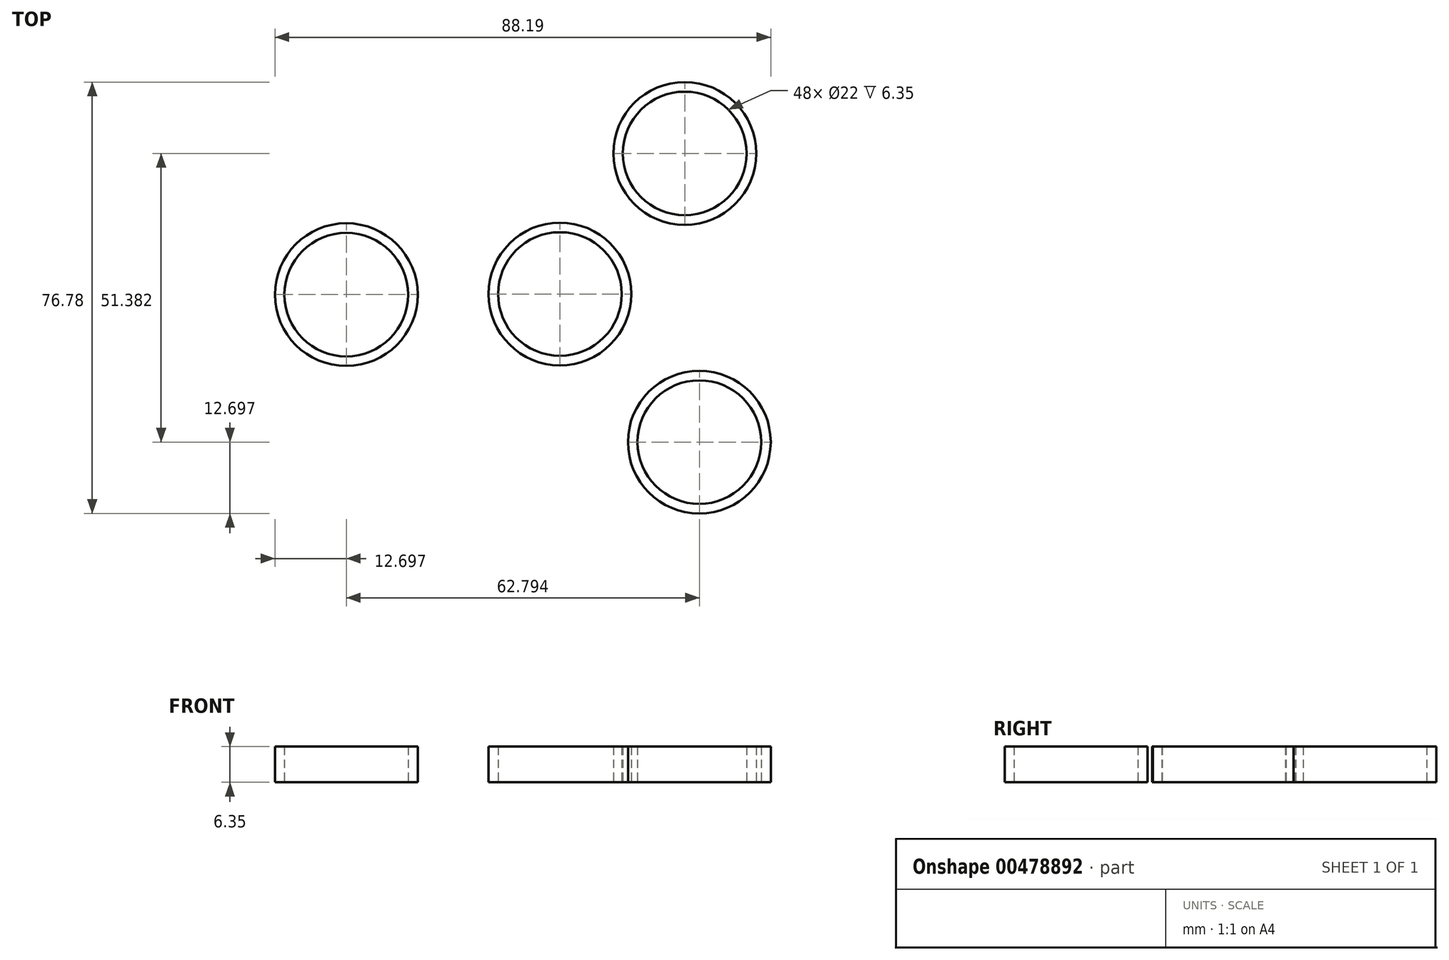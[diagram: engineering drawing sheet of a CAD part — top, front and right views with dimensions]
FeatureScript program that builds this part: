
annotation { "Feature Type Name" : "Feature", "Feature Type Description" : "" }
export const myFeature = defineFeature(function(context is Context, id is Id, definition is map)
    precondition{}
    {
        {
            var Q0;
            Q0=qCreatedBy(makeId("Top.planeOp"),FACE);
            var sketch = newSketch(context, id + "F0", { "sketchPlane" : qUnion([Q0])});
            skCircle(sketch, "E0", {"center": v(-0.39, 0.25) * mm, "radius": 12.7 * mm});
            skCircle(sketch, "E1", {"center": v(-0.39, 0.25) * mm, "radius": 11 * mm});
            skCircle(sketch, "E2", {"center": v(21.82, 25.27) * mm, "radius": 11 * mm});
            skCircle(sketch, "E3", {"center": v(21.82, 25.27) * mm, "radius": 12.7 * mm});
            skCircle(sketch, "E4", {"center": v(24.41, -26.11) * mm, "radius": 11 * mm});
            skCircle(sketch, "E5", {"center": v(24.41, -26.11) * mm, "radius": 12.7 * mm});
            skCircle(sketch, "E6", {"center": v(-38.38, 0.14) * mm, "radius": 11 * mm});
            skCircle(sketch, "E7", {"center": v(-38.38, 0.14) * mm, "radius": 12.7 * mm});
            skSolve(sketch);
        }
        {
            var Q0;
            Q0 = qSketchRegion(id + "F0", true);
            extrude(context, id + "F1", {"entities" : qUnion([Q0]), "depth" : 6.35 * mm});
        }
    });
